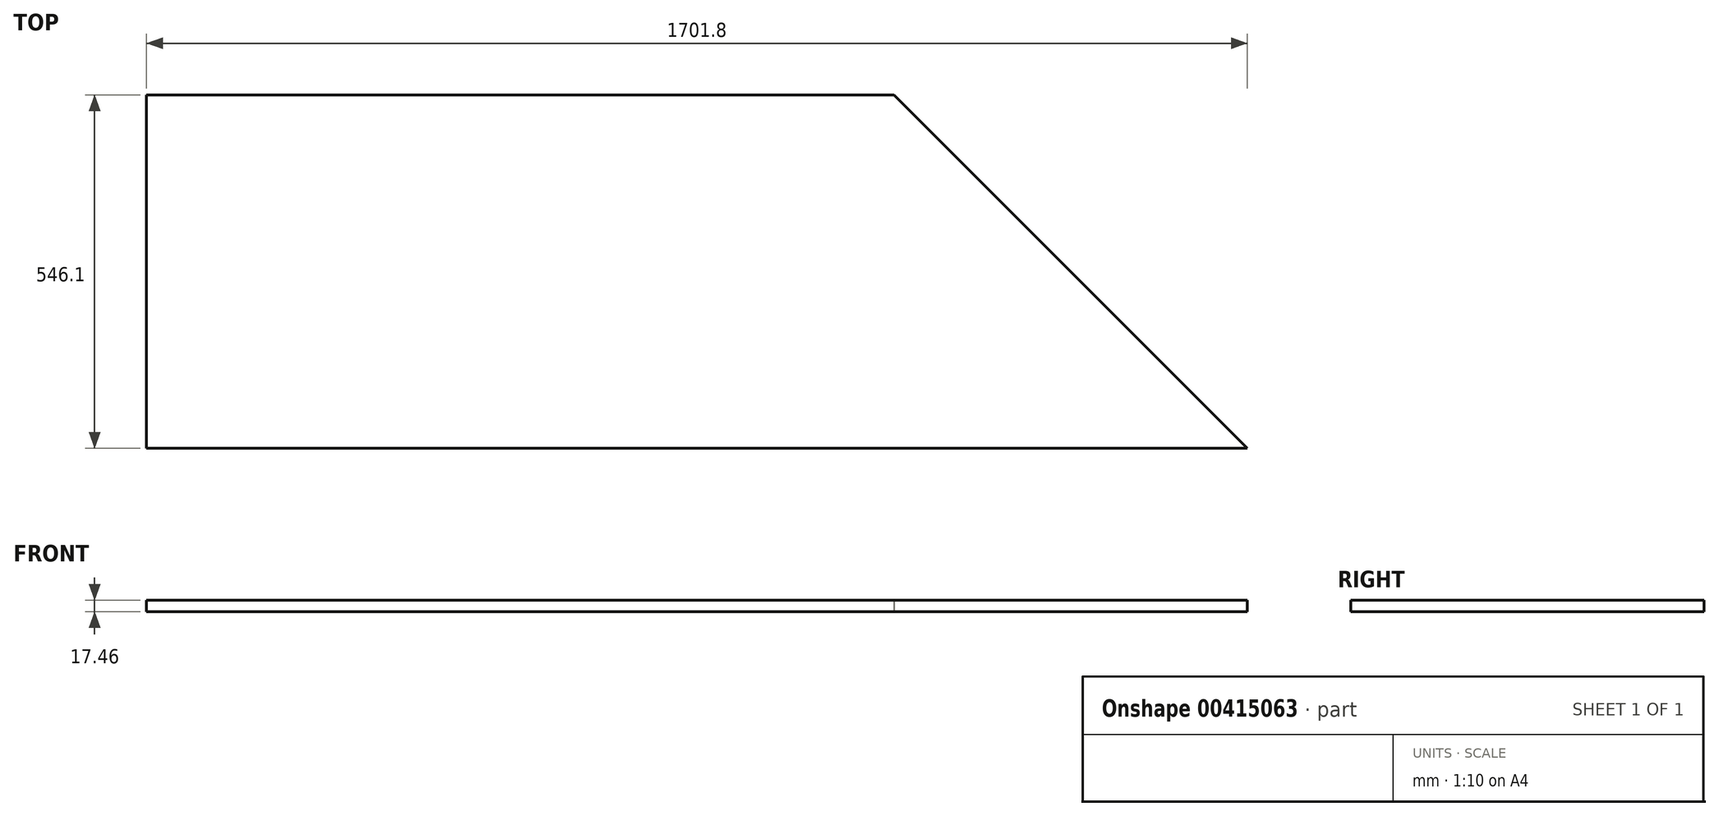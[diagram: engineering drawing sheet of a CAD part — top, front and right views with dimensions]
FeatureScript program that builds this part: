
annotation { "Feature Type Name" : "Feature", "Feature Type Description" : "" }
export const myFeature = defineFeature(function(context is Context, id is Id, definition is map)
    precondition{}
    {
        {
            var Q0;
            Q0=qCreatedBy(makeId("Top.planeOp"),FACE);
            var sketch = newSketch(context, id + "F0", { "sketchPlane" : qUnion([Q0])});
            skLineSegment(sketch, "E0", {"start": v(0, 0) * mm, "end": v(1701.8, 0) * mm});
            skLineSegment(sketch, "E1", {"start": v(1701.8, 0) * mm, "end": v(1155.7, 546.1) * mm});
            skLineSegment(sketch, "E2", {"start": v(1155.7, 546.1) * mm, "end": v(0, 546.1) * mm});
            skLineSegment(sketch, "E3", {"start": v(0, 546.1) * mm, "end": v(0, 0) * mm});
            skSolve(sketch);
        }
        {
            var Q0;
            Q0=makeQuery(id+"F0.imprint","IMPRINT",FACE,{"disambiguationData":[TD([[makeQuery(id+"F0.imprint","IMPRINT",EDGE,{"derivedFrom":sQuery(id+"F0.wireOp",EDGE,"E0")}),1.0]])]});
            extrude(context, id + "F1", {"entities" : qUnion([Q0]), "depth" : 17.46 * mm, "offsetDistance" : 25.4 * mm});
        }
    });
